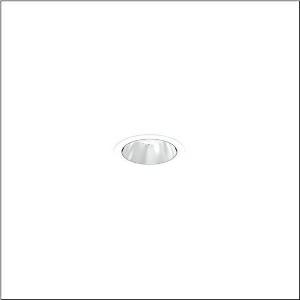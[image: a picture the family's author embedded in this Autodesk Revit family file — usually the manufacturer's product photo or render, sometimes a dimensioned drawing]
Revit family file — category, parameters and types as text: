
# Revit family: lunis_21_s_51db15ma91c
name_source: partatom
category: Lighting Fixtures
units: mm (PartAtom-declared; Revit-internal decimal feet)

## family parameters
Cut with Voids When Loaded = No
Host = Face
Light Source = No
Part Type = Normal
Room Calculation Point = No
Round Connector Dimension = Use Diameter
Shared = No

## types (1)
- --- (1 x LED, 980 lm, 5.9 W, 6500K)
    Apparent Load = 6 VA
    CIE Flux Codes = 93 99 100 100 100
    Color Rendering = 80
    Color Temperature = 6500K
    Default Elevation = 1800 mm
    Description = Lunis 21,  S, downlight, light control with lens, of PMMA, anti glare with reflector, of PC, highly specular, light emission: direct distribution, LED rated luminous flux: 990lm, light colour: 830/840/865, with terminal, 3-pole, mains connection: 220..240V, AC, 50..60Hz, housing, round, of diecast aluminium, traffic white (RAL 9016), diameter: 84mm, clamping range: 1..40mm, protection rating (complete): IP20, protection rating (on room side): IP54, insulation class (complete): insulation class II (safety insulation), certification: CE, impact resistance: IK03, packaging unit: 1 piece
    Height = 0 mm  [stored 0 ft]
    Lamp = 1 x LED
    Lamp Light Flux = 980 lm
    Lamp Power = 5.9 W
    Lamp count = 1
    Length = 84 mm
    Luminous efficacy = 166 lm/W
    Manufacturer = Siteco
    ModVariant = No
    Model = 51DB15MA91C
    Mounting Place = Ceiling
    Mounting Type = Recessed
    Number of Poles = 1
    OnlyDefault = Yes
    Power Factor = 1
    Product Name = Lunis 21 S
    Product group = downlight
    ProductGroupID = 400
    Protection Class = Protection class II
    Protection Degree = IP 20
    RLX_Detail_Level = 1
    RLX_Emergency_Light_Flux = 0 lm
    RLX_Emergency_Type = 0
    RLX_Emergency_Type_DB = No
    RlxData = <blob elided: 8365 chars, md5=ac2a725d>
    Socket = socket
    Standby Power = 0 W
    System Light Flux = 980 lm
    System Power = 6 W
    Type Comments = individual setting: colour temperature 6500K
    Type Image = l_1290840.jpg
    URL = http://relux.com
    VarID = @adj_020750
    Voltage = 0 V
    Weight = 0.00 kg
    Width = 0 mm  [stored 0 ft]

note: [stored X ft] marks values corroborated as IEEE doubles in the binary element streams (Revit-internal decimal feet)

## geometry (parser evidence)
native form markers: Sweep x10
no freeform markers — native parametric forms only
